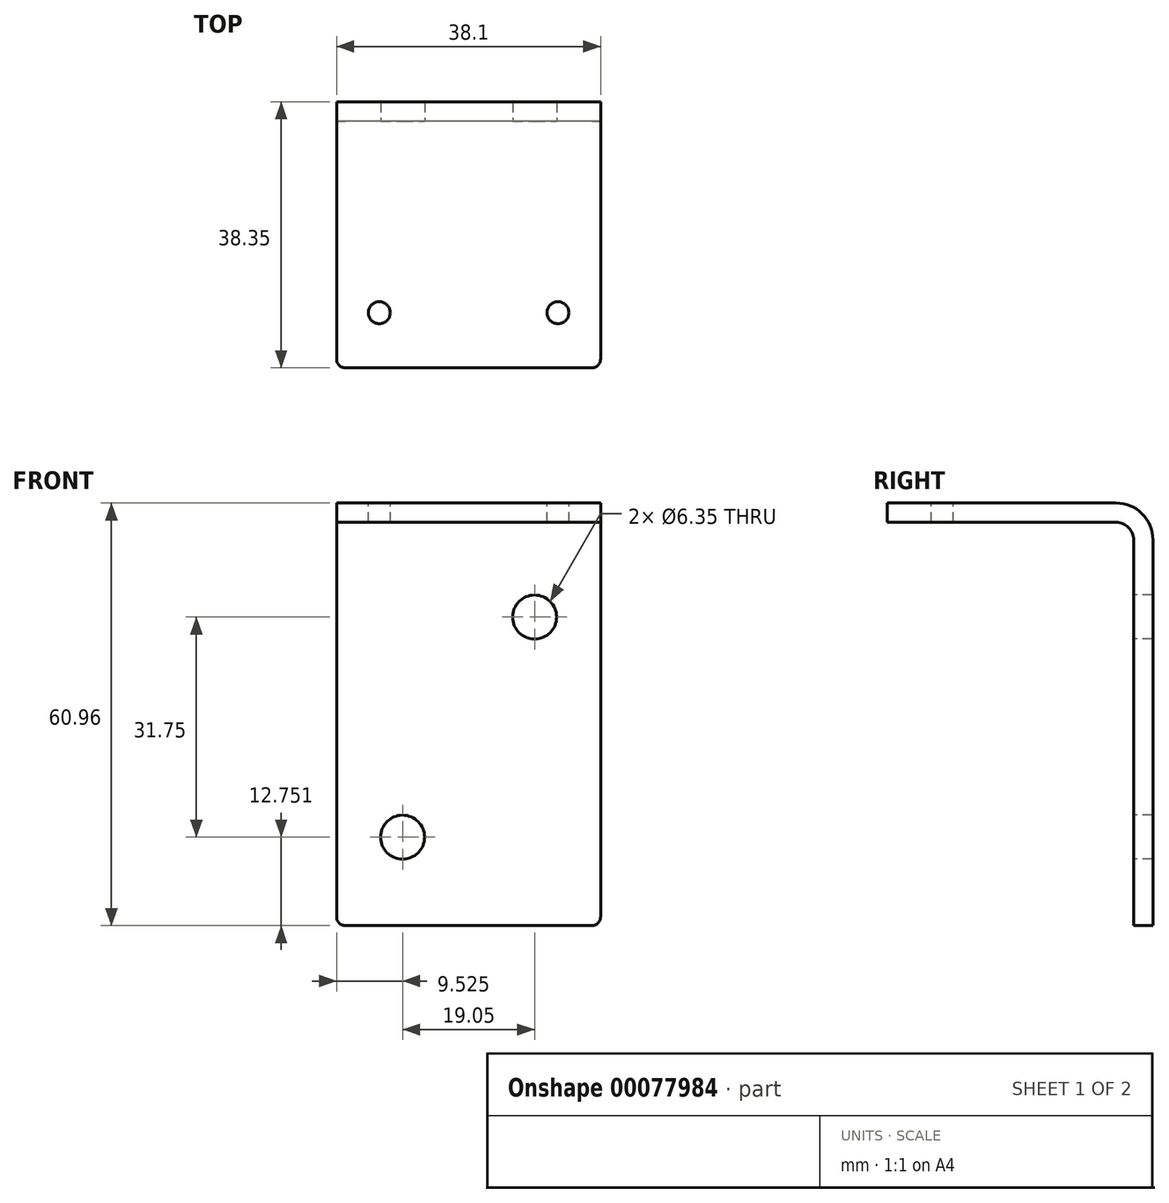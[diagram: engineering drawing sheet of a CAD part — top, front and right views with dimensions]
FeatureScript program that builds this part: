
annotation { "Feature Type Name" : "Feature", "Feature Type Description" : "" }
export const myFeature = defineFeature(function(context is Context, id is Id, definition is map)
    precondition{}
    {
        {
            var Q0;
            Q0=qCreatedBy(makeId("Right.planeOp"),FACE);
            var sketch = newSketch(context, id + "F0", { "sketchPlane" : qUnion([Q0])});
            skLineSegment(sketch, "E0.bottom", {"start": v(0, 0) * mm, "end": v(-2.8, 0) * mm});
            skLineSegment(sketch, "E0.left", {"start": v(0, 0) * mm, "end": v(0, 55.63) * mm});
            skLineSegment(sketch, "E0.right", {"start": v(-2.8, 0) * mm, "end": v(-2.8, 55.63) * mm});
            skLineSegment(sketch, "E1.top", {"start": v(-5.33, 58.17) * mm, "end": v(-38.35, 58.17) * mm});
            skLineSegment(sketch, "E1.right", {"start": v(-38.35, 60.96) * mm, "end": v(-38.35, 58.17) * mm});
            skPoint(sketch, "E2.visualSharp", {"position": v(-2.8, 58.17) * mm});
            skArc(sketch, "E2.filletArc", {"start": v(-2.8, 55.63) * mm, "mid": v(-3.54, 57.42) * mm, "end": v(-5.33, 58.17) * mm});
            skLineSegment(sketch, "E3", {"start": v(-38.35, 60.96) * mm, "end": v(-5.33, 60.96) * mm});
            skPoint(sketch, "E4.visualSharp", {"position": v(0, 60.96) * mm});
            skArc(sketch, "E4.filletArc", {"start": v(0, 55.63) * mm, "mid": v(-1.56, 59.4) * mm, "end": v(-5.33, 60.96) * mm});
            skSolve(sketch);
        }
        {
            var Q0;
            Q0=qSketchRegion(id+"F0",true);
            extrude(context, id + "F1", {"entities" : qUnion([Q0]), "depth" : 38.1 * mm});
        }
        {
            var Q0;
            Q0=makeQuery(id+"F1.opExtrude","CAP_EDGE",EDGE,{"disambiguationData":[OSD([sQuery(id+"F0.wireOp",EDGE,"E1.right")])],"isStart":true});
            var Q1;
            Q1=makeQuery(id+"F1.opExtrude","CAP_EDGE",EDGE,{"disambiguationData":[OSD([sQuery(id+"F0.wireOp",EDGE,"E1.right")])],"isStart":false});
            var Q2;
            Q2=makeQuery(id+"F1.opExtrude","CAP_EDGE",EDGE,{"disambiguationData":[OSD([sQuery(id+"F0.wireOp",EDGE,"E0.bottom")])],"isStart":false});
            var Q3;
            Q3=makeQuery(id+"F1.opExtrude","CAP_EDGE",EDGE,{"disambiguationData":[OSD([sQuery(id+"F0.wireOp",EDGE,"E0.bottom")])],"isStart":true});
            fillet(context, id + "F2", {"entities" : qUnion([Q0, Q1, Q2, Q3]), "radius" : 1.27 * mm, "tangentPropagation" : true, "allowEdgeOverflow" : false});
        }
        {
            var Q0;
            Q0=makeQuery(id+"F1.opExtrude","SWEPT_FACE",FACE,{"disambiguationData":[OSD([sQuery(id+"F0.wireOp",EDGE,"E3")])]});
            var sketch = newSketch(context, id + "F3", { "sketchPlane" : qUnion([Q0])});
            skLineSegment(sketch, "E5", {"start": v(19.05, -38.35) * mm, "end": v(19.05, -5.33) * mm, "construction": true});
            skCircle(sketch, "E6", {"center": v(19.05, -26.29) * mm, "radius": 2.54 * mm, "construction": true});
            skCircle(sketch, "E7", {"center": v(31.94, -30.4) * mm, "radius": 1.59 * mm});
            skCircle(sketch, "E8", {"center": v(6.16, -30.4) * mm, "radius": 1.59 * mm});
            skLineSegment(sketch, "E9", {"start": v(0, -30.4) * mm, "end": v(38.1, -30.4) * mm, "construction": true});
            skSolve(sketch);
        }
        {
            var Q0;
            Q0=qSketchRegion(id+"F3",true);
            extrude(context, id + "F4", {"entities" : qUnion([Q0]), "operationType" : NewBodyOperationType.REMOVE, "endBound" : BoundingType.UP_TO_NEXT, "oppositeDirection" : true, "depth" : 25.4 * mm});
        }
        {
            var Q0;
            Q0=makeQuery(id+"F1.opExtrude","SWEPT_FACE",FACE,{"disambiguationData":[OSD([sQuery(id+"F0.wireOp",EDGE,"E0.right")])]});
            var sketch = newSketch(context, id + "F5", { "sketchPlane" : qUnion([Q0])});
            skCircle(sketch, "E10", {"center": v(28.58, 44.5) * mm, "radius": 3.18 * mm});
            skCircle(sketch, "E11", {"center": v(9.53, 12.75) * mm, "radius": 3.18 * mm});
            skLineSegment(sketch, "E12", {"start": v(38.1, 44.5) * mm, "end": v(28.58, 44.5) * mm, "construction": true});
            skLineSegment(sketch, "E13", {"start": v(0, 12.75) * mm, "end": v(9.53, 12.75) * mm, "construction": true});
            skLineSegment(sketch, "E14", {"start": v(9.53, 12.75) * mm, "end": v(9.53, 0) * mm, "construction": true});
            skLineSegment(sketch, "E15", {"start": v(28.58, 44.5) * mm, "end": v(28.58, 55.63) * mm, "construction": true});
            skSolve(sketch);
        }
        {
            var Q0;
            Q0=qSketchRegion(id+"F5",true);
            extrude(context, id + "F6", {"entities" : qUnion([Q0]), "operationType" : NewBodyOperationType.REMOVE, "endBound" : BoundingType.UP_TO_NEXT, "oppositeDirection" : true, "depth" : 25.4 * mm});
        }
    });
